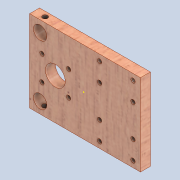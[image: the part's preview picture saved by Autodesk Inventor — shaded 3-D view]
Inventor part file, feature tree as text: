
AUTODESK INVENTOR PART (.ipt)
format: ipt  version: 2020 (Build 240168000, 168)  size: 297,984 bytes
history: native  units: mm
features: sketch x7, other x6, extrude x4, hole x3, pattern_linear x2, reference x2, direct_edit x1, move_body x1
ambient origin geometry x8: Origin, YZ Plane, XZ Plane, XY Plane, X Axis, Y Axis, Z Axis, Center Point
bodies: Solid1 (feature_tree)
feature tree (26):
  extrude  "Extrusion1"  Depth=66.0mm
  extrude  "Extrusion4"  TaperAngle=0.0deg  [1 undecoded]
  extrude  "Extrusion5"  TaperAngle=0.0deg  [1 undecoded]
  extrude  "Extrusion6"  Depth=9.0mm
  sketch  "Sketch7"  dims[d27=8.5mm d28=9.0mm]
  hole  "Hole1"  [1 undecoded]
  direct_edit  "Direct Edit1"
  pattern_linear  "Rectangular Pattern2"  Spacing1=3.5mm  [1 undecoded]
  pattern_linear  "Rectangular Pattern3"  Spacing1=21.5mm  [1 undecoded]
  hole  "Hole2"  [1 undecoded]
  hole  "Hole3"  [1 undecoded]
  sketch  "Sketch1"  dims[d0=87.5mm d1=66.0mm]
  sketch  "Sketch4"  dims[d2=8.0mm d3=0.0mm d19=0.0mm d20=0.0mm]
  sketch  "Sketch6"  dims[d24=16.0mm d25=0.0mm d26=0.0mm]
  sketch  "Sketch8"  dims[d29=10.8mm d30=9.0mm]
  reference  "Reference7"
  reference  "Reference8"
  sketch  "Sketch10"  dims[d31=0.0mm d32=0.0mm]
  sketch  "Sketch11"  dims[d33=20.748842mm d35=3.5mm d36=21.5mm d37=20.0mm d38=4.0mm d39=5.0mm d40=15.0mm d41=5.0mm d42=15.0mm d43=3.5mm d44=6.0mm d45=4.0mm d46=2.0mm d47=90.0deg d48=8.0mm d49=20.594885mm d53=0.0mm d54=0.0mm d55=2.0mm d56=26.0mm d57=20.0mm d59=15.0mm d60=20.0mm d62=41.0mm d63=20.0mm d65=27.0mm d66=8.5mm d67=4.134mm d68=5.0mm d69=4.0mm d70=2.0mm d71=90.0deg d72=7.45mm d73=20.594885mm d74=8.5mm d75=4.134mm d76=5.0mm d77=4.0mm d78=2.0mm d79=90.0deg d80=7.45mm d81=20.594885mm]
  parser-record x1  (decoder bookkeeping rows leaked as tree rows — omitted from the tree; the rows remain in map.json)
  other  "0005-00-00 Ansamblu_General.iam"
  other  "Surub M4 saiba piulita.iam:65"
  other  "0005-10-1013 ISO 7089 - 4 - 140 HV.ipt:2"
  move_body  "Move1"
  other  "0005-10-04 Z axis and extruder.iam"
  other  "0005-10-1002  Hub.ipt:22"
note: 7 required parameter values undecoded (feature->parameter linkage not recoverable at this tier; creation-order binding heuristic only, values carry confidence <= 0.55)
note: 1 file-system path scrubbed to <path> (originals preserved in map.json)
